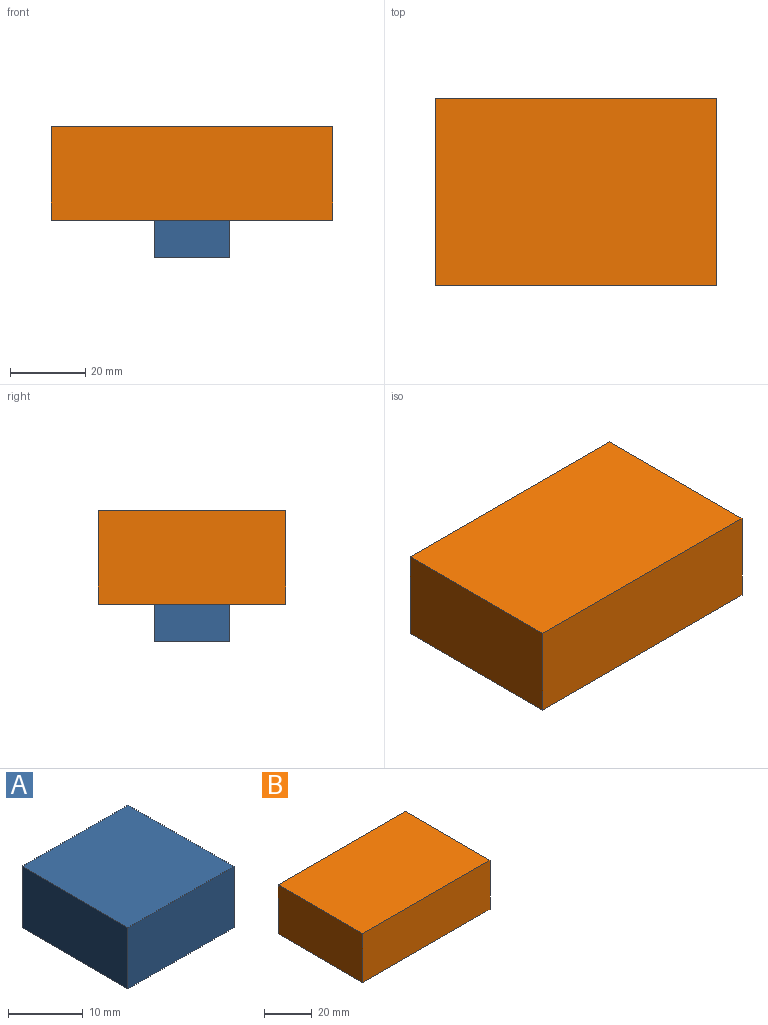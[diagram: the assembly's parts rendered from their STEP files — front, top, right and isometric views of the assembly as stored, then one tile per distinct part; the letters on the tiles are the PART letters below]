
ASSEMBLY  parts=2 mates=1
PART A: 6 faces, bbox 20x20x10 mm
  f0: plane 20x10mm, normal (0,1,0), area 200mm2, adj f1,f3,f4,f5
  f1: plane 20x10mm, normal (-1,0,0), area 200mm2, adj f0,f2,f4,f5
  f2: plane 20x10mm, normal (0,-1,0), area 200mm2, adj f1,f3,f4,f5
  f3: plane 20x10mm, normal (1,0,0), area 200mm2, adj f0,f2,f4,f5
  f4: plane 20x20mm, normal (0,0,1), area 400mm2, adj f0,f1,f2,f3
  f5: plane 20x20mm, normal (0,0,-1), area 400mm2, adj f0,f1,f2,f3
PART B: 6 faces, bbox 75x50x25 mm
  f0: plane 75x25mm, normal (0,1,0), area 1875mm2, adj f1,f3,f4,f5
  f1: plane 50x25mm, normal (-1,0,0), area 1250mm2, adj f0,f2,f4,f5
  f2: plane 75x25mm, normal (0,-1,0), area 1875mm2, adj f1,f3,f4,f5
  f3: plane 50x25mm, normal (1,0,0), area 1250mm2, adj f0,f2,f4,f5
  f4: plane 75x50mm, normal (0,0,1), area 3750mm2, adj f0,f1,f2,f3
  f5: plane 75x50mm, normal (0,0,-1), area 3750mm2, adj f0,f1,f2,f3
PLACE A t=(-14.82,10.5,2.3)mm
PLACE B t=(-2.32,10.5,12.3)mm
MATE planar A.f4 <-> B.f5  axis (0,0,1) through (-14.82,10.5,12.3)mm
